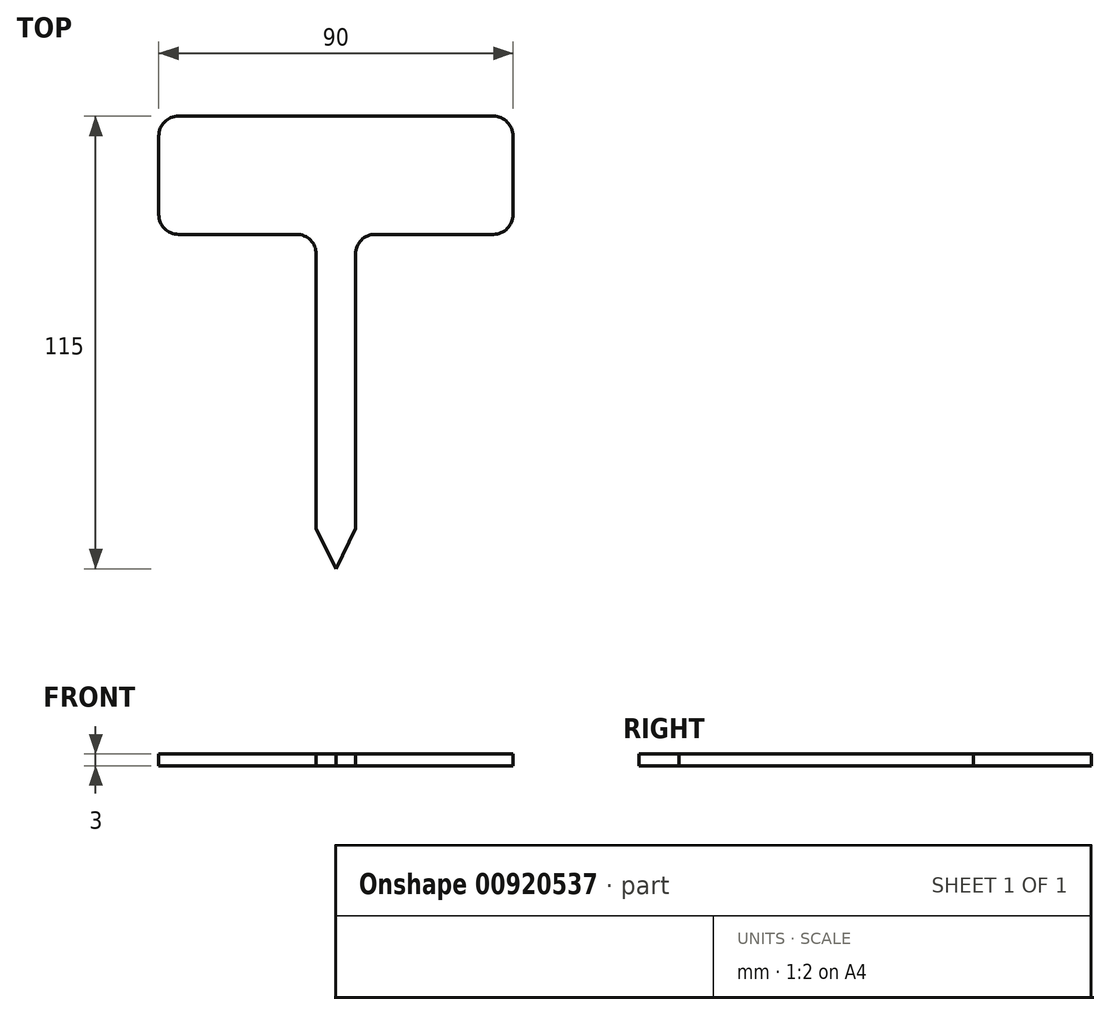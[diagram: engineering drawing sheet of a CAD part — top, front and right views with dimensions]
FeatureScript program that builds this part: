
annotation { "Feature Type Name" : "Feature", "Feature Type Description" : "" }
export const myFeature = defineFeature(function(context is Context, id is Id, definition is map)
    precondition{}
    {
        {
            var Q0;
            Q0=qCreatedBy(makeId("Top.planeOp"),FACE);
            var sketch = newSketch(context, id + "F0", { "sketchPlane" : qUnion([Q0])});
            skLineSegment(sketch, "E0.bottom", {"start": v(-45, 30) * mm, "end": v(45, 30) * mm});
            skLineSegment(sketch, "E0.top", {"start": v(-45, 0) * mm, "end": v(45, 0) * mm});
            skLineSegment(sketch, "E0.left", {"start": v(-45, 30) * mm, "end": v(-45, 0) * mm});
            skLineSegment(sketch, "E0.right", {"start": v(45, 30) * mm, "end": v(45, 0) * mm});
            skLineSegment(sketch, "E1.bottom", {"start": v(-5, 0) * mm, "end": v(5, 0) * mm});
            skLineSegment(sketch, "E1.top", {"start": v(-5, -85) * mm, "end": v(5, -85) * mm});
            skLineSegment(sketch, "E1.left", {"start": v(-5, 0) * mm, "end": v(-5, -85) * mm});
            skLineSegment(sketch, "E1.right", {"start": v(5, 0) * mm, "end": v(5, -85) * mm});
            skSolve(sketch);
        }
        {
            var Q0;
            Q0=makeQuery(id+"F0.imprint","IMPRINT",FACE,{"disambiguationData":[TD([[makeQuery(id+"F0.imprint","IMPRINT",EDGE,{"derivedFrom":sQuery(id+"F0.wireOp",EDGE,"hWdg1ORp-hpeX-Rt3e-eoev-cJ3iOh7CwEnP.bottom")}),-1.0]])]});
            var Q1;
            Q1=makeQuery(id+"F0.imprint","IMPRINT",FACE,{"disambiguationData":[TD([[makeQuery(id+"F0.imprint","IMPRINT",EDGE,{"derivedFrom":sQuery(id+"F0.wireOp",EDGE,"E0.bottom")}),-1.0]])]});
            var Q2;
            Q2=makeQuery(id+"F0.imprint","IMPRINT",FACE,{"disambiguationData":[TD([[makeQuery(id+"F0.imprint","IMPRINT",EDGE,{"derivedFrom":sQuery(id+"F0.wireOp",EDGE,"E1.top")}),1.0]])]});
            extrude(context, id + "F1", {"entities" : qUnion([Q0, Q1, Q2]), "depth" : 3 * mm, "offsetDistance" : 25 * mm});
        }
        {
            var Q0;
            Q0=makeQuery(id+"F1.opExtrude","SWEPT_EDGE",EDGE,{"disambiguationData":[OSD([sQuery(id+"F0.wireOp",EDGE,"E0.top"),sQuery(id+"F0.wireOp",EDGE,"E0.left")])]});
            var Q1;
            Q1=makeQuery(id+"F1.opExtrude","SWEPT_EDGE",EDGE,{"disambiguationData":[OSD([sQuery(id+"F0.wireOp",EDGE,"E0.bottom"),sQuery(id+"F0.wireOp",EDGE,"E0.left")])]});
            var Q2;
            Q2=makeQuery(id+"F1.opExtrude","SWEPT_EDGE",EDGE,{"disambiguationData":[OSD([sQuery(id+"F0.wireOp",EDGE,"E0.top"),sQuery(id+"F0.wireOp",EDGE,"E0.right")])]});
            var Q3;
            Q3=makeQuery(id+"F1.opExtrude","SWEPT_EDGE",EDGE,{"disambiguationData":[OSD([sQuery(id+"F0.wireOp",EDGE,"E0.bottom"),sQuery(id+"F0.wireOp",EDGE,"E0.right")])]});
            var Q4;
            Q4=makeQuery(id+"F1.opExtrude","SWEPT_EDGE",EDGE,{"disambiguationData":[OSD([sQuery(id+"F0.wireOp",EDGE,"E0.top"),sQuery(id+"F0.wireOp",EDGE,"E1.right")])]});
            var Q5;
            Q5=makeQuery(id+"F1.opExtrude","SWEPT_EDGE",EDGE,{"disambiguationData":[OSD([sQuery(id+"F0.wireOp",EDGE,"E0.top"),sQuery(id+"F0.wireOp",EDGE,"E1.left")])]});
            fillet(context, id + "F2", {"entities" : qUnion([Q0, Q1, Q2, Q3, Q4, Q5]), "radius" : 5 * mm, "tangentPropagation" : true, "allowEdgeOverflow" : false});
        }
        {
            var Q0;
            Q0=makeQuery(id+"F1.opExtrude","CAP_FACE",FACE,{"disambiguationData":[OSD([sQuery(id+"F0.wireOp",EDGE,"E0.bottom"),sQuery(id+"F0.wireOp",EDGE,"E0.top"),sQuery(id+"F0.wireOp",EDGE,"E0.left"),sQuery(id+"F0.wireOp",EDGE,"E0.right"),sQuery(id+"F0.wireOp",EDGE,"E1.top"),sQuery(id+"F0.wireOp",EDGE,"E1.left"),sQuery(id+"F0.wireOp",EDGE,"E1.right")])],"isStart":false});
            var sketch = newSketch(context, id + "F3", { "sketchPlane" : qUnion([Q0])});
            skLineSegment(sketch, "E2", {"start": v(0, -85) * mm, "end": v(-5, -74.8) * mm});
            skLineSegment(sketch, "E3.MirrorCS", {"start": v(0, -85) * mm, "end": v(5, -74.8) * mm});
            skSolve(sketch);
        }
        {
            var Q0;
            Q0 = qSketchRegion(id + "F3", true);
            var Q1;
            {var subQ0=sQuery(id+"F3.wireOp",EDGE,"E2");Q1=makeQuery(id+"F3.imprint","IMPRINT",FACE,{"disambiguationData":[TD([[makeQuery(id+"F3.imprint","IMPRINT",EDGE,{"derivedFrom":subQ0}),1.0]])]});}
            var Q2;
            {var subQ0=sQuery(id+"F3.wireOp",EDGE,"E3.MirrorCS");Q2=makeQuery(id+"F3.imprint","IMPRINT",FACE,{"disambiguationData":[TD([[makeQuery(id+"F3.imprint","IMPRINT",EDGE,{"derivedFrom":subQ0}),-1.0]])]});}
            extrude(context, id + "F4", {"entities" : qUnion([Q0, Q1, Q2]), "operationType" : NewBodyOperationType.REMOVE, "oppositeDirection" : true, "depth" : 25 * mm, "offsetDistance" : 25 * mm});
        }
    });
